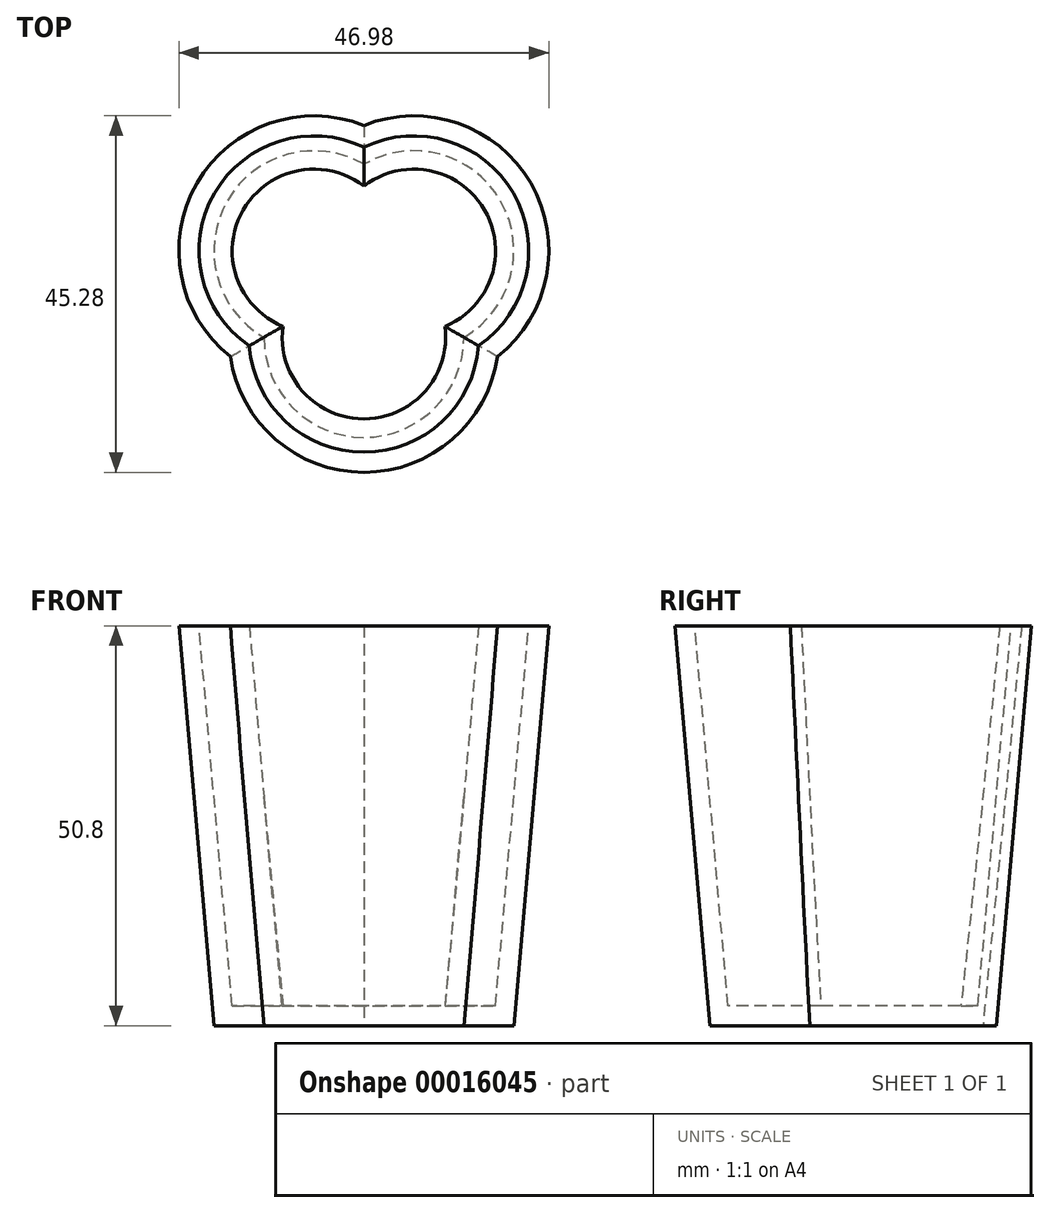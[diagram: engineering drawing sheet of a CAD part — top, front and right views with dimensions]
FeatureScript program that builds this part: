
annotation { "Feature Type Name" : "Feature", "Feature Type Description" : "" }
export const myFeature = defineFeature(function(context is Context, id is Id, definition is map)
    precondition{}
    {
        {
            var Q0;
            Q0=qCreatedBy(makeId("Top.planeOp"),FACE);
            var sketch = newSketch(context, id + "F0", { "sketchPlane" : qUnion([Q0])});
            skCircle(sketch, "E0", {"center": v(0, 0) * mm, "radius": 12.7 * mm});
            skCircle(sketch, "E1", {"center": v(12.7, 0) * mm, "radius": 12.7 * mm});
            skCircle(sketch, "E2", {"center": v(6.35, -11) * mm, "radius": 12.7 * mm});
            skSolve(sketch);
        }
        {
            var Q0;
            {var subQ0=sQuery(id+"F0.wireOp",EDGE,"E2");var subQ3=sQuery(id+"F0.wireOp",EDGE,"E0");var subQ4=makeQuery(id+"F0.imprint","INTERSECT",VERTEX,{"disambiguationData":[OD(0.0)],"derivedFrom":[subQ3,subQ0]});Q0=makeQuery(id+"F0.imprint","IMPRINT",FACE,{"disambiguationData":[TD([[makeQuery(id+"F0.imprint","IMPRINT",EDGE,{"disambiguationData":[TD([[subQ4,-1.0]])],"derivedFrom":subQ3}),-1.0]])]});}
            var Q1;
            {var subQ0=sQuery(id+"F0.wireOp",EDGE,"E2");var subQ3=sQuery(id+"F0.wireOp",EDGE,"E0");var subQ4=makeQuery(id+"F0.imprint","INTERSECT",VERTEX,{"disambiguationData":[OD(1.0)],"derivedFrom":[subQ3,subQ0]});Q1=makeQuery(id+"F0.imprint","IMPRINT",FACE,{"disambiguationData":[TD([[makeQuery(id+"F0.imprint","IMPRINT",EDGE,{"disambiguationData":[TD([[subQ4,1.0]])],"derivedFrom":subQ3}),1.0]])]});}
            var Q2;
            {var subQ1=sQuery(id+"F0.wireOp",EDGE,"E0");var subQ3=sQuery(id+"F0.wireOp",EDGE,"E1");var subQ5=makeQuery(id+"F0.imprint","INTERSECT",VERTEX,{"disambiguationData":[OD(0.0)],"derivedFrom":[subQ1,subQ3]});Q2=makeQuery(id+"F0.imprint","IMPRINT",FACE,{"disambiguationData":[TD([[makeQuery(id+"F0.imprint","IMPRINT",EDGE,{"disambiguationData":[TD([[subQ5,1.0]])],"derivedFrom":subQ1}),-1.0]])]});}
            var Q3;
            {var subQ1=sQuery(id+"F0.wireOp",EDGE,"E1");var subQ3=sQuery(id+"F0.wireOp",EDGE,"E0");var subQ5=makeQuery(id+"F0.imprint","INTERSECT",VERTEX,{"disambiguationData":[OD(0.0)],"derivedFrom":[subQ3,subQ1]});Q3=makeQuery(id+"F0.imprint","IMPRINT",FACE,{"disambiguationData":[TD([[makeQuery(id+"F0.imprint","IMPRINT",EDGE,{"disambiguationData":[TD([[subQ5,1.0]])],"derivedFrom":subQ3}),1.0]])]});}
            var Q4;
            {var subQ0=sQuery(id+"F0.wireOp",EDGE,"E2");var subQ1=sQuery(id+"F0.wireOp",EDGE,"E0");var subQ2=makeQuery(id+"F0.imprint","INTERSECT",VERTEX,{"disambiguationData":[OD(1.0)],"derivedFrom":[subQ1,subQ0]});Q4=makeQuery(id+"F0.imprint","IMPRINT",FACE,{"disambiguationData":[TD([[makeQuery(id+"F0.imprint","IMPRINT",EDGE,{"disambiguationData":[TD([[subQ2,1.0]])],"derivedFrom":subQ1}),-1.0]])]});}
            var Q5;
            {var subQ1=sQuery(id+"F0.wireOp",EDGE,"E1");var subQ3=sQuery(id+"F0.wireOp",EDGE,"E0");var subQ5=makeQuery(id+"F0.imprint","INTERSECT",VERTEX,{"disambiguationData":[OD(0.0)],"derivedFrom":[subQ3,subQ1]});Q5=makeQuery(id+"F0.imprint","IMPRINT",FACE,{"disambiguationData":[TD([[makeQuery(id+"F0.imprint","IMPRINT",EDGE,{"disambiguationData":[TD([[subQ5,-1.0]])],"derivedFrom":subQ3}),1.0]])]});}
            var Q6;
            {var subQ0=sQuery(id+"F0.wireOp",EDGE,"E2");var subQ3=sQuery(id+"F0.wireOp",EDGE,"E0");var subQ4=makeQuery(id+"F0.imprint","INTERSECT",VERTEX,{"disambiguationData":[OD(0.0)],"derivedFrom":[subQ3,subQ0]});Q6=makeQuery(id+"F0.imprint","IMPRINT",FACE,{"disambiguationData":[TD([[makeQuery(id+"F0.imprint","IMPRINT",EDGE,{"disambiguationData":[TD([[subQ4,-1.0]])],"derivedFrom":subQ3}),1.0]])]});}
            extrude(context, id + "F1", {"entities" : qUnion([Q0, Q1, Q2, Q3, Q4, Q5, Q6]), "depth" : 50.8 * mm, "hasDraft" : true, "draftAngle" : 5 * degree});
        }
        {
            var Q0;
            Q0=makeQuery(id+"F1.opExtrude","CAP_FACE",FACE,{"disambiguationData":[OSD([sQuery(id+"F0.wireOp",EDGE,"E0"),sQuery(id+"F0.wireOp",EDGE,"E1"),sQuery(id+"F0.wireOp",EDGE,"E2")])],"isStart":false});
            shell(context, id + "F2", {"entities" : qUnion([Q0]), "thickness" : 2.54 * mm});
        }
    });
